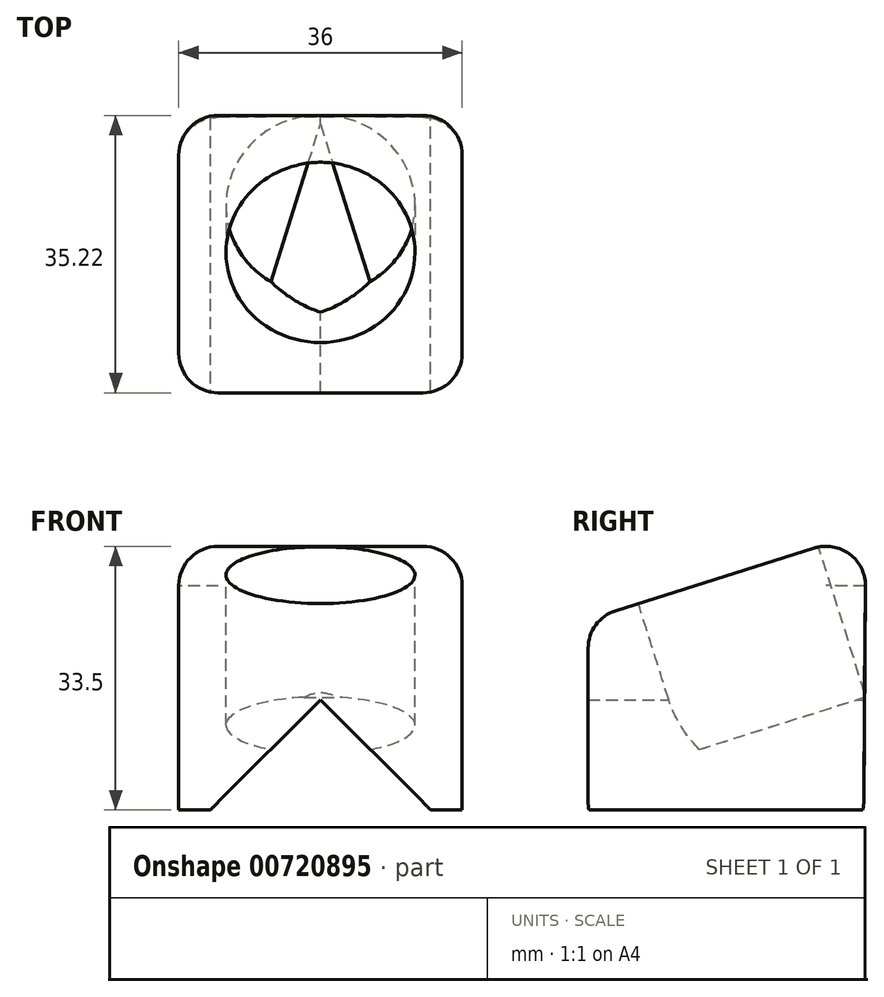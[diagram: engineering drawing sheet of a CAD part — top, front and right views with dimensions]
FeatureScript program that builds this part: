
annotation { "Feature Type Name" : "Feature", "Feature Type Description" : "" }
export const myFeature = defineFeature(function(context is Context, id is Id, definition is map)
    precondition{}
    {
        {
            var Q0;
            Q0=qCreatedBy(makeId("Right.planeOp"),FACE);
            var sketch = newSketch(context, id + "F0", { "sketchPlane" : qUnion([Q0])});
            skLineSegment(sketch, "E0", {"start": v(17.4, -16.5) * mm, "end": v(-17.6, -16.5) * mm});
            skLineSegment(sketch, "E1", {"start": v(-17.6, -16.5) * mm, "end": v(-17.6, 7.71) * mm});
            skLineSegment(sketch, "E2", {"start": v(-17.6, 7.71) * mm, "end": v(17.68, 18.84) * mm});
            skLineSegment(sketch, "E3", {"start": v(17.68, 18.84) * mm, "end": v(17.4, -16.5) * mm});
            skSolve(sketch);
        }
        {
            var Q0;
            Q0=makeQuery(id+"F0.imprint","IMPRINT",FACE,{"disambiguationData":[TD([[makeQuery(id+"F0.imprint","IMPRINT",EDGE,{"derivedFrom":sQuery(id+"F0.wireOp",EDGE,"E0")}),-1.0]])]});
            extrude(context, id + "F1", {"entities" : qUnion([Q0]), "endBound" : BoundingType.SYMMETRIC, "depth" : 36 * mm, "offsetDistance" : 25 * mm});
        }
        {
            var Q0;
            Q0=makeQuery(id+"F1.opExtrude","SWEPT_FACE",FACE,{"disambiguationData":[OSD([sQuery(id+"F0.wireOp",EDGE,"E2")])]});
            var sketch = newSketch(context, id + "F2", { "sketchPlane" : qUnion([Q0])});
            skCircle(sketch, "E4", {"center": v(0, 4.24) * mm, "radius": 12 * mm});
            skSolve(sketch);
        }
        {
            var Q0;
            Q0=makeQuery(id+"F2.imprint","IMPRINT",FACE,{"disambiguationData":[TD([[makeQuery(id+"F2.imprint","IMPRINT",EDGE,{"derivedFrom":sQuery(id+"F2.wireOp",EDGE,"E4")}),1.0]])]});
            extrude(context, id + "F3", {"entities" : qUnion([Q0]), "operationType" : NewBodyOperationType.REMOVE, "oppositeDirection" : true, "depth" : 20 * mm, "offsetDistance" : 25 * mm});
        }
        {
            var Q0;
            Q0=qCreatedBy(makeId("Front.planeOp"),FACE);
            var sketch = newSketch(context, id + "F4", { "sketchPlane" : qUnion([Q0])});
            skLineSegment(sketch, "E5", {"start": v(0, -2.5) * mm, "end": v(-18.38, -20.89) * mm});
            skLineSegment(sketch, "E6", {"start": v(-18.38, -20.89) * mm, "end": v(0, -39.27) * mm});
            skLineSegment(sketch, "E7", {"start": v(0, -39.27) * mm, "end": v(18.38, -20.89) * mm});
            skLineSegment(sketch, "E8", {"start": v(18.38, -20.89) * mm, "end": v(0, -2.5) * mm});
            skSolve(sketch);
        }
        {
            var Q0;
            Q0=makeQuery(id+"F4.imprint","IMPRINT",FACE,{"disambiguationData":[TD([[makeQuery(id+"F4.imprint","IMPRINT",EDGE,{"derivedFrom":sQuery(id+"F4.wireOp",EDGE,"E5")}),1.0]])]});
            extrude(context, id + "F5", {"entities" : qUnion([Q0]), "operationType" : NewBodyOperationType.REMOVE, "endBound" : BoundingType.SYMMETRIC, "depth" : 38 * mm, "offsetDistance" : 25 * mm});
        }
        {
            var Q0;
            Q0=makeQuery(id+"F1.opExtrude","CAP_EDGE",EDGE,{"disambiguationData":[OSD([sQuery(id+"F0.wireOp",EDGE,"E1")])],"isStart":true});
            var Q1;
            Q1=makeQuery(id+"F1.opExtrude","SWEPT_EDGE",EDGE,{"disambiguationData":[OSD([sQuery(id+"F0.wireOp",EDGE,"E1"),sQuery(id+"F0.wireOp",EDGE,"E2")])]});
            var Q2;
            Q2=makeQuery(id+"F1.opExtrude","CAP_EDGE",EDGE,{"disambiguationData":[OSD([sQuery(id+"F0.wireOp",EDGE,"E2")])],"isStart":true});
            var Q3;
            Q3=makeQuery(id+"F1.opExtrude","CAP_EDGE",EDGE,{"disambiguationData":[OSD([sQuery(id+"F0.wireOp",EDGE,"E2")])],"isStart":false});
            var Q4;
            Q4=makeQuery(id+"F1.opExtrude","CAP_EDGE",EDGE,{"disambiguationData":[OSD([sQuery(id+"F0.wireOp",EDGE,"E1")])],"isStart":false});
            var Q5;
            Q5=makeQuery(id+"F1.opExtrude","CAP_EDGE",EDGE,{"disambiguationData":[OSD([sQuery(id+"F0.wireOp",EDGE,"E3")])],"isStart":false});
            var Q6;
            Q6=makeQuery(id+"F1.opExtrude","CAP_EDGE",EDGE,{"disambiguationData":[OSD([sQuery(id+"F0.wireOp",EDGE,"E3")])],"isStart":true});
            var Q7;
            Q7=makeQuery(id+"F1.opExtrude","SWEPT_EDGE",EDGE,{"disambiguationData":[OSD([sQuery(id+"F0.wireOp",EDGE,"E2"),sQuery(id+"F0.wireOp",EDGE,"E3")])]});
            fillet(context, id + "F6", {"entities" : qUnion([Q0, Q1, Q2, Q3, Q4, Q5, Q6, Q7]), "radius" : 5 * mm, "tangentPropagation" : true, "allowEdgeOverflow" : false});
        }
    });
